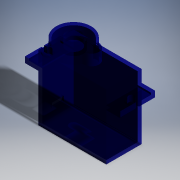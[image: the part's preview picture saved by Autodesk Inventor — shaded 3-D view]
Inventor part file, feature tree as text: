
AUTODESK INVENTOR PART (.ipt)
format: ipt  version: 2016 (Build 200138000, 138)  size: 435,712 bytes
history: native  units: in
note: dims shown in document units (in); Inventor stores cm internally (conversion verified against a paired STEP export)
features: fillet x21, extrude x8, sketch x8, shell x1
ambient origin geometry x8: Origin, YZ Plane, XZ Plane, XY Plane, X Axis, Y Axis, Z Axis, Center Point
bodies: Solid1 (feature_tree)
feature tree (38):
  extrude  "Extrusion1"  Depth=0.6299in
  extrude  "Extrusion2"  Depth=0.4724in
  extrude  "Extrusion3"  Depth=0.0787in TaperAngle=0.0deg
  extrude  "Extrusion4"  Depth=0.4724in
  extrude  "Extrusion5"  Depth=0.0787in
  extrude  "Extrusion6"  Depth=0.1654in TaperAngle=0.0deg
  extrude  "Extrusion7"  Depth=0.1969in
  shell  "Shell1"  Thickness=0.1181in
  extrude  "Extrusion8"  Depth=0.0079in
  fillet  "Fillet1"  Radius=0.0591in
  fillet  "Fillet2"  Radius=0.1378in
  fillet  "Fillet3"  Radius=0.1181in
  fillet  "Fillet4"  Radius=0.0197in
  fillet  "Fillet5"  Radius=0.0197in
  fillet  "Fillet6"  Radius=0.0197in
  fillet  "Fillet7"  Radius=0.0079in
  fillet  "Fillet8"  Radius=0.0079in
  fillet  "Fillet9"  Radius=0.0079in
  fillet  "Fillet10"  Radius=0.0079in
  fillet  "Fillet11"  Radius=0.0079in
  fillet  "Fillet12"  Radius=0.0079in
  fillet  "Fillet13"  Radius=0.0079in
  fillet  "Fillet14"  Radius=0.0079in
  fillet  "Fillet15"  Radius=0.0079in
  fillet  "Fillet16"  Radius=0.0079in
  fillet  "Fillet17"  Radius=0.0079in
  fillet  "Fillet18"  Radius=0.0079in
  fillet  "Fillet19"  Radius=0.0039in
  fillet  "Fillet20"  Radius=0.0039in
  fillet  "Fillet21"  Radius=0.0079in
  sketch  "Sketch1"  dims[d0=0.9055in d1=0.6299in]
  sketch  "Sketch2"  dims[d2=0.4724in d3=0.0in d4=1.2598in]
  sketch  "Sketch3"  dims[d5=0.4724in d6=0.0787in d7=0.0in]
  sketch  "Sketch4"  dims[d8=0.9055in d9=0.4724in]
  sketch  "Sketch5"  dims[d10=0.1575in d11=0.0in d12=0.0787in]
  sketch  "Sketch6"  dims[d16=0.1654in d17=0.0in d22=0.1654in d23=0.0in]
  sketch  "Sketch7"  dims[d27=0.1654in d28=0.0in d29=0.1969in d30=0.1181in d31=0.0in]
  sketch  "Sketch8"  dims[d32=0.0276in d33=0.1575in d34=0.0591in d35=0.1378in d36=0.1181in d37=0.0in d38=0.0197in d39=0.0197in d40=0.0197in d41=0.0079in d42=0.0079in d43=0.0079in d44=0.0079in d45=0.0079in d46=0.0079in d47=0.0079in d48=0.0079in d49=0.0079in d50=0.0079in d51=0.0079in d52=0.0079in d53=0.0039in d54=0.0039in d55=0.0079in d56=0.0079in d57=0.0079in d58=0.0079in]
